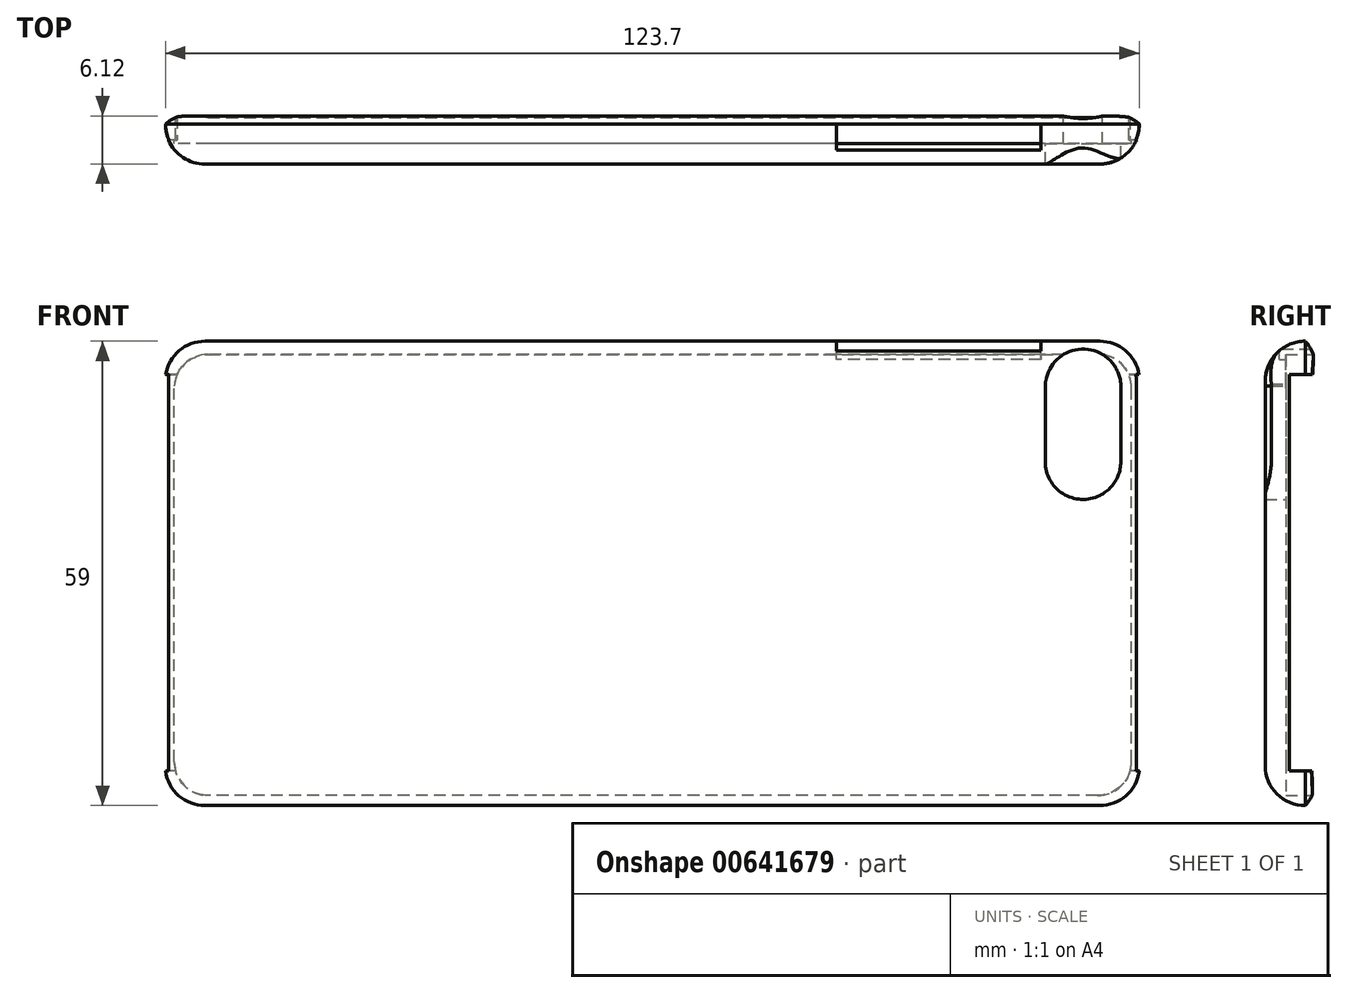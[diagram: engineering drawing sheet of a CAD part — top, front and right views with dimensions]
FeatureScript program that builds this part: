
annotation { "Feature Type Name" : "Feature", "Feature Type Description" : "" }
export const myFeature = defineFeature(function(context is Context, id is Id, definition is map)
    precondition{}
    {
        {
            var Q0;
            Q0=qCreatedBy(makeId("Front.planeOp"),FACE);
            var sketch = newSketch(context, id + "F0", { "sketchPlane" : qUnion([Q0])});
            skLineSegment(sketch, "E0.bottom", {"start": v(-63.83, -59.89) * mm, "end": v(59.97, -59.89) * mm});
            skLineSegment(sketch, "E0.top", {"start": v(-63.83, -118.89) * mm, "end": v(59.97, -118.89) * mm});
            skLineSegment(sketch, "E0.left", {"start": v(-63.83, -59.89) * mm, "end": v(-63.83, -118.89) * mm});
            skLineSegment(sketch, "E0.right", {"start": v(59.97, -59.89) * mm, "end": v(59.97, -118.89) * mm});
            skSolve(sketch);
        }
        {
            var Q0;
            Q0=makeQuery(id+"F0.imprint","IMPRINT",FACE,{"disambiguationData":[TD([[makeQuery(id+"F0.imprint","IMPRINT",EDGE,{"derivedFrom":sQuery(id+"F0.wireOp",EDGE,"E0.bottom")}),-1.0]])]});
            extrude(context, id + "F1", {"entities" : qUnion([Q0]), "depth" : 6.4 * mm, "offsetDistance" : 25.4 * mm});
        }
        {
            var Q0;
            Q0=makeQuery(id+"F1.opExtrude","CAP_EDGE",EDGE,{"disambiguationData":[OSD([sQuery(id+"F0.wireOp",EDGE,"E0.left")])],"isStart":false});
            var Q1;
            Q1=makeQuery(id+"F1.opExtrude","CAP_EDGE",EDGE,{"disambiguationData":[OSD([sQuery(id+"F0.wireOp",EDGE,"E0.bottom")])],"isStart":false});
            var Q2;
            Q2=makeQuery(id+"F1.opExtrude","CAP_EDGE",EDGE,{"disambiguationData":[OSD([sQuery(id+"F0.wireOp",EDGE,"E0.right")])],"isStart":false});
            var Q3;
            Q3=makeQuery(id+"F1.opExtrude","CAP_EDGE",EDGE,{"disambiguationData":[OSD([sQuery(id+"F0.wireOp",EDGE,"E0.top")])],"isStart":false});
            fillet(context, id + "F2", {"entities" : qUnion([Q0, Q1, Q2, Q3]), "radius" : 5.08 * mm, "tangentPropagation" : true, "allowEdgeOverflow" : false});
        }
        {
            var Q0;
            Q0=qCreatedBy(makeId("Front.planeOp"),FACE);
            var sketch = newSketch(context, id + "F3", { "sketchPlane" : qUnion([Q0])});
            skArc(sketch, "E1", {"start": v(57.57, -65.36) * mm, "mid": v(52.65, -60.9) * mm, "end": v(47.97, -65.6) * mm});
            skLineSegment(sketch, "E2", {"start": v(47.97, -65.6) * mm, "end": v(47.97, -75.2) * mm});
            skLineSegment(sketch, "E3", {"start": v(57.57, -65.36) * mm, "end": v(57.57, -75.2) * mm});
            skArc(sketch, "E4", {"start": v(47.97, -75.2) * mm, "mid": v(52.77, -80) * mm, "end": v(57.57, -75.2) * mm});
            skSolve(sketch);
        }
        {
            var Q0;
            Q0 = qSketchRegion(id + "F3", true);
            extrude(context, id + "F4", {"entities" : qUnion([Q0]), "operationType" : NewBodyOperationType.REMOVE, "depth" : 59.94 * mm, "offsetDistance" : 25.4 * mm});
        }
        {
            var Q0;
            Q0=qCreatedBy(makeId("Front.planeOp"),FACE);
            var sketch = newSketch(context, id + "F5", { "sketchPlane" : qUnion([Q0])});
            skLineSegment(sketch, "E5.bottom", {"start": v(58.92, -61.58) * mm, "end": v(-62.67, -61.58) * mm});
            skLineSegment(sketch, "E5.top", {"start": v(58.92, -117.6) * mm, "end": v(-62.67, -117.6) * mm});
            skLineSegment(sketch, "E5.left", {"start": v(58.92, -61.58) * mm, "end": v(58.92, -117.6) * mm});
            skLineSegment(sketch, "E5.right", {"start": v(-62.67, -61.58) * mm, "end": v(-62.67, -117.6) * mm});
            skSolve(sketch);
        }
        {
            var Q0;
            Q0 = qSketchRegion(id + "F5", true);
            extrude(context, id + "F6", {"entities" : qUnion([Q0]), "operationType" : NewBodyOperationType.REMOVE, "depth" : 3.8 * mm, "offsetDistance" : 25.4 * mm});
        }
        {
            var Q0;
            Q0=makeQuery(id+"F6.boolean.opBoolean","COPY",EDGE,{"derivedFrom":makeQuery(id+"F6.opExtrude","SWEPT_EDGE",EDGE,{"disambiguationData":[OSD([sQuery(id+"F5.wireOp",EDGE,"E5.bottom"),sQuery(id+"F5.wireOp",EDGE,"E5.left")])]})});
            var Q1;
            Q1=makeQuery(id+"F6.boolean.opBoolean","COPY",EDGE,{"derivedFrom":makeQuery(id+"F6.opExtrude","SWEPT_EDGE",EDGE,{"disambiguationData":[OSD([sQuery(id+"F5.wireOp",EDGE,"E5.top"),sQuery(id+"F5.wireOp",EDGE,"E5.left")])]})});
            var Q2;
            Q2=makeQuery(id+"F6.boolean.opBoolean","COPY",EDGE,{"derivedFrom":makeQuery(id+"F6.opExtrude","SWEPT_EDGE",EDGE,{"disambiguationData":[OSD([sQuery(id+"F5.wireOp",EDGE,"E5.top"),sQuery(id+"F5.wireOp",EDGE,"E5.right")])]})});
            var Q3;
            Q3=makeQuery(id+"F6.boolean.opBoolean","COPY",EDGE,{"derivedFrom":makeQuery(id+"F6.opExtrude","SWEPT_EDGE",EDGE,{"disambiguationData":[OSD([sQuery(id+"F5.wireOp",EDGE,"E5.bottom"),sQuery(id+"F5.wireOp",EDGE,"E5.right")])]})});
            fillet(context, id + "F7", {"entities" : qUnion([Q0, Q1, Q2, Q3]), "radius" : 4.3 * mm, "tangentPropagation" : true, "allowEdgeOverflow" : false});
        }
        {
            var Q0;
            Q0=makeQuery(id+"F1.opExtrude","SWEPT_EDGE",EDGE,{"disambiguationData":[OSD([sQuery(id+"F0.wireOp",EDGE,"E0.top"),sQuery(id+"F0.wireOp",EDGE,"E0.right")])]});
            var Q1;
            Q1=makeQuery(id+"F1.opExtrude","SWEPT_EDGE",EDGE,{"disambiguationData":[OSD([sQuery(id+"F0.wireOp",EDGE,"E0.top"),sQuery(id+"F0.wireOp",EDGE,"E0.left")])]});
            var Q2;
            Q2=makeQuery(id+"F1.opExtrude","SWEPT_EDGE",EDGE,{"disambiguationData":[OSD([sQuery(id+"F0.wireOp",EDGE,"E0.bottom"),sQuery(id+"F0.wireOp",EDGE,"E0.left")])]});
            var Q3;
            Q3=makeQuery(id+"F1.opExtrude","SWEPT_EDGE",EDGE,{"disambiguationData":[OSD([sQuery(id+"F0.wireOp",EDGE,"E0.bottom"),sQuery(id+"F0.wireOp",EDGE,"E0.right")])]});
            fillet(context, id + "F8", {"entities" : qUnion([Q0, Q1, Q2, Q3]), "radius" : 5.08 * mm, "tangentPropagation" : true, "allowEdgeOverflow" : false});
        }
        {
            var Q0;
            Q0=qCreatedBy(makeId("Top.planeOp"),FACE);
            var sketch = newSketch(context, id + "F9", { "sketchPlane" : qUnion([Q0])});
            skPoint(sketch, "E6.left.start.orphan", {"position": v(21.47, 0) * mm});
            skLineSegment(sketch, "E7", {"start": v(21.47, -1.32) * mm, "end": v(47.41, -1.32) * mm});
            skPoint(sketch, "E6.top.end.orphan", {"position": v(47.41, -3.32) * mm});
            skLineSegment(sketch, "E8", {"start": v(47.41, -4.62) * mm, "end": v(21.47, -4.62) * mm});
            skLineSegment(sketch, "E9", {"start": v(21.47, -4.62) * mm, "end": v(21.47, -1.32) * mm});
            skLineSegment(sketch, "E10", {"start": v(47.41, -1.32) * mm, "end": v(47.41, -4.62) * mm});
            skSolve(sketch);
        }
        {
            var Q0;
            Q0 = qSketchRegion(id + "F9", true);
            extrude(context, id + "F10", {"entities" : qUnion([Q0]), "operationType" : NewBodyOperationType.REMOVE, "oppositeDirection" : true, "depth" : 62.23 * mm, "offsetDistance" : 25.4 * mm});
        }
        {
            var Q0;
            Q0=qCreatedBy(makeId("Right.planeOp"),FACE);
            var sketch = newSketch(context, id + "F11", { "sketchPlane" : qUnion([Q0])});
            skLineSegment(sketch, "E11.bottom", {"start": v(0, -64.13) * mm, "end": v(-3.34, -64.13) * mm});
            skLineSegment(sketch, "E11.top", {"start": v(0, -114.5) * mm, "end": v(-3.34, -114.5) * mm});
            skLineSegment(sketch, "E11.left", {"start": v(0, -64.13) * mm, "end": v(0, -114.5) * mm});
            skLineSegment(sketch, "E11.right", {"start": v(-3.34, -64.13) * mm, "end": v(-3.34, -114.5) * mm});
            skSolve(sketch);
        }
        {
            var Q0;
            Q0 = qSketchRegion(id + "F11", true);
            extrude(context, id + "F12", {"entities" : qUnion([Q0]), "operationType" : NewBodyOperationType.REMOVE, "endBound" : BoundingType.SYMMETRIC, "depth" : 155.45 * mm, "offsetDistance" : 25.4 * mm});
        }
        {
            var Q0;
            Q0=makeQuery(id+"F1.opExtrude","CAP_EDGE",EDGE,{"disambiguationData":[OSD([sQuery(id+"F0.wireOp",EDGE,"E0.bottom")])],"isStart":true});
            var Q1;
            {var subQ0=sQuery(id+"F0.wireOp",EDGE,"E0.left");var subQ1=sQuery(id+"F0.wireOp",EDGE,"E0.bottom");Q1=makeQuery(id+"F8.opFillet","BLEND_EDGE",EDGE,{"blendedFrom":[makeQuery(id+"F1.opExtrude","SWEPT_EDGE",EDGE,{"disambiguationData":[OSD([subQ1,subQ0])]}),makeQuery(id+"F1.opExtrude","CAP_FACE",FACE,{"disambiguationData":[OSD([subQ1,sQuery(id+"F0.wireOp",EDGE,"E0.top"),subQ0,sQuery(id+"F0.wireOp",EDGE,"E0.right")])],"isStart":true})],"blendedInto":[makeQuery(id+"F1.opExtrude","CAP_FACE",FACE,{"disambiguationData":[OSD([subQ1,sQuery(id+"F0.wireOp",EDGE,"E0.top"),subQ0,sQuery(id+"F0.wireOp",EDGE,"E0.right")])],"isStart":true})]});}
            var Q2;
            {var subQ0=sQuery(id+"F0.wireOp",EDGE,"E0.right");var subQ1=sQuery(id+"F0.wireOp",EDGE,"E0.bottom");Q2=makeQuery(id+"F8.opFillet","BLEND_EDGE",EDGE,{"blendedFrom":[makeQuery(id+"F1.opExtrude","SWEPT_EDGE",EDGE,{"disambiguationData":[OSD([subQ1,subQ0])]}),makeQuery(id+"F1.opExtrude","CAP_FACE",FACE,{"disambiguationData":[OSD([subQ1,sQuery(id+"F0.wireOp",EDGE,"E0.top"),sQuery(id+"F0.wireOp",EDGE,"E0.left"),subQ0])],"isStart":true})],"blendedInto":[makeQuery(id+"F1.opExtrude","CAP_FACE",FACE,{"disambiguationData":[OSD([subQ1,sQuery(id+"F0.wireOp",EDGE,"E0.top"),sQuery(id+"F0.wireOp",EDGE,"E0.left"),subQ0])],"isStart":true})]});}
            var Q3;
            {var subQ0=sQuery(id+"F0.wireOp",EDGE,"E0.right");var subQ1=sQuery(id+"F0.wireOp",EDGE,"E0.top");Q3=makeQuery(id+"F8.opFillet","BLEND_EDGE",EDGE,{"blendedFrom":[makeQuery(id+"F1.opExtrude","SWEPT_EDGE",EDGE,{"disambiguationData":[OSD([subQ1,subQ0])]}),makeQuery(id+"F1.opExtrude","CAP_FACE",FACE,{"disambiguationData":[OSD([sQuery(id+"F0.wireOp",EDGE,"E0.bottom"),subQ1,sQuery(id+"F0.wireOp",EDGE,"E0.left"),subQ0])],"isStart":true})],"blendedInto":[makeQuery(id+"F1.opExtrude","CAP_FACE",FACE,{"disambiguationData":[OSD([sQuery(id+"F0.wireOp",EDGE,"E0.bottom"),subQ1,sQuery(id+"F0.wireOp",EDGE,"E0.left"),subQ0])],"isStart":true})]});}
            var Q4;
            Q4=makeQuery(id+"F1.opExtrude","CAP_EDGE",EDGE,{"disambiguationData":[OSD([sQuery(id+"F0.wireOp",EDGE,"E0.top")])],"isStart":true});
            var Q5;
            {var subQ0=sQuery(id+"F0.wireOp",EDGE,"E0.left");var subQ1=sQuery(id+"F0.wireOp",EDGE,"E0.top");Q5=makeQuery(id+"F8.opFillet","BLEND_EDGE",EDGE,{"blendedFrom":[makeQuery(id+"F1.opExtrude","SWEPT_EDGE",EDGE,{"disambiguationData":[OSD([subQ1,subQ0])]}),makeQuery(id+"F2.opFillet","BLEND_EDGE",EDGE,{"blendedFrom":[makeQuery(id+"F1.opExtrude","CAP_EDGE",EDGE,{"disambiguationData":[OSD([subQ1])],"isStart":false}),makeQuery(id+"F1.opExtrude","CAP_EDGE",EDGE,{"disambiguationData":[OSD([subQ0])],"isStart":false})],"blendedInto":[]})],"blendedInto":[]});}
            var Q6;
            {var subQ0=sQuery(id+"F0.wireOp",EDGE,"E0.left");var subQ1=sQuery(id+"F0.wireOp",EDGE,"E0.top");Q6=makeQuery(id+"F8.opFillet","BLEND_EDGE",EDGE,{"blendedFrom":[makeQuery(id+"F1.opExtrude","SWEPT_EDGE",EDGE,{"disambiguationData":[OSD([subQ1,subQ0])]}),makeQuery(id+"F1.opExtrude","CAP_FACE",FACE,{"disambiguationData":[OSD([sQuery(id+"F0.wireOp",EDGE,"E0.bottom"),subQ1,subQ0,sQuery(id+"F0.wireOp",EDGE,"E0.right")])],"isStart":true})],"blendedInto":[makeQuery(id+"F1.opExtrude","CAP_FACE",FACE,{"disambiguationData":[OSD([sQuery(id+"F0.wireOp",EDGE,"E0.bottom"),subQ1,subQ0,sQuery(id+"F0.wireOp",EDGE,"E0.right")])],"isStart":true})]});}
            fillet(context, id + "F13", {"entities" : qUnion([Q0, Q1, Q2, Q3, Q4, Q5, Q6]), "radius" : 5.08 * mm, "tangentPropagation" : true, "allowEdgeOverflow" : false});
        }
    });
